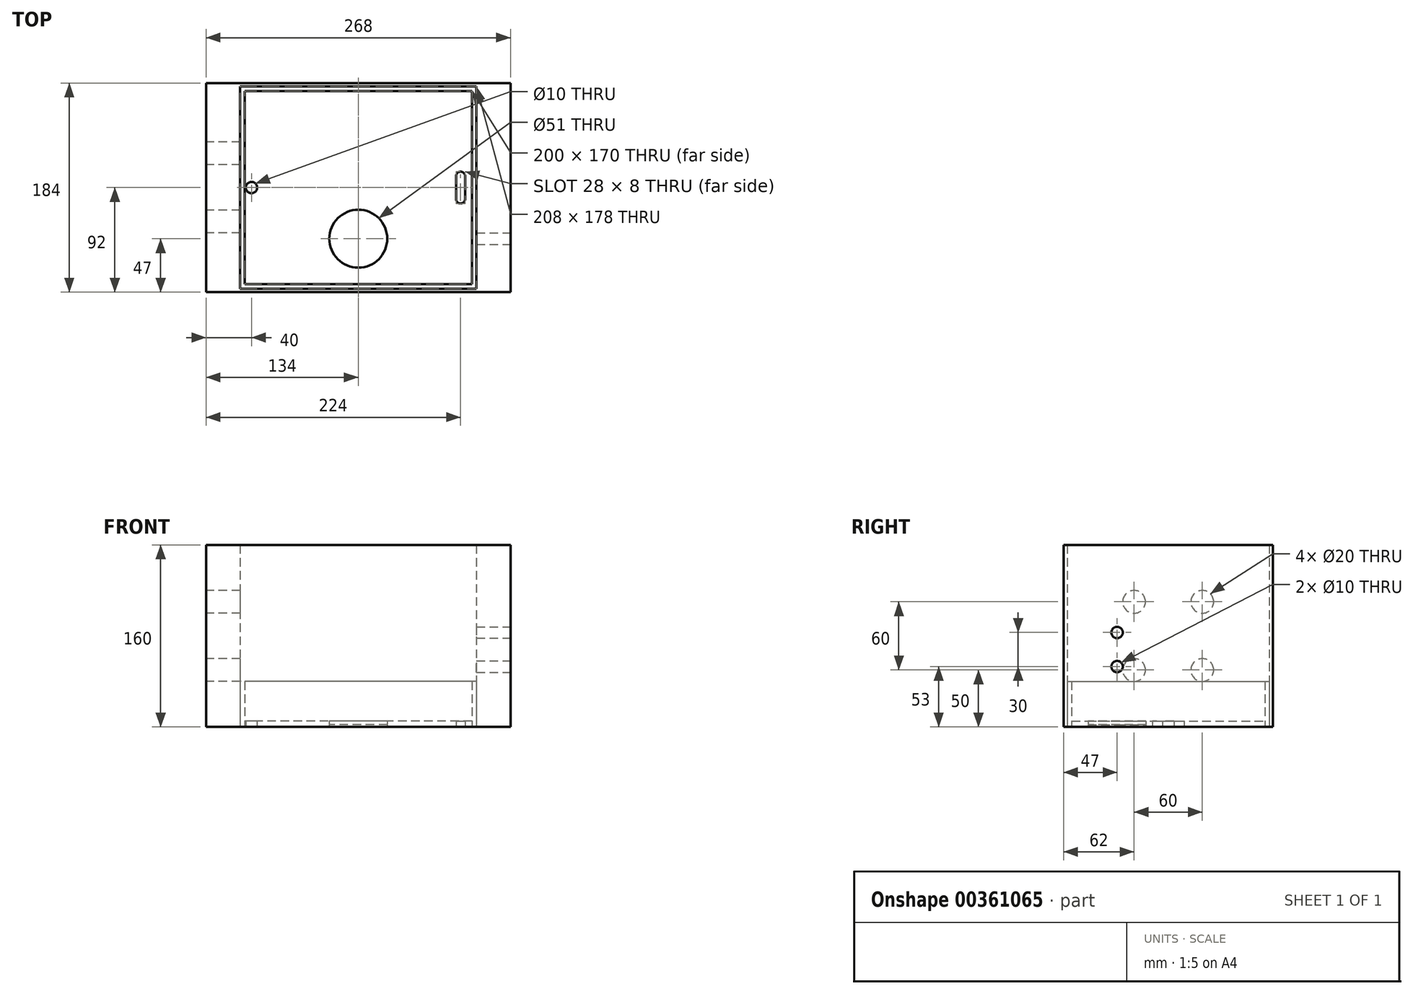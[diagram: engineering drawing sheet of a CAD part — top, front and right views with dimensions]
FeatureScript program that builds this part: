
annotation { "Feature Type Name" : "Feature", "Feature Type Description" : "" }
export const myFeature = defineFeature(function(context is Context, id is Id, definition is map)
    precondition{}
    {
        {
            var Q0;
            Q0=qCreatedBy(makeId("Top.planeOp"),FACE);
            var sketch = newSketch(context, id + "F0", { "sketchPlane" : qUnion([Q0])});
            skLineSegment(sketch, "E0.bottom", {"start": v(134, -47) * mm, "end": v(-134, -47) * mm});
            skLineSegment(sketch, "E0.top", {"start": v(134, 137) * mm, "end": v(-134, 137) * mm});
            skPoint(sketch, "E0.middle", {"position": v(0, 0) * mm});
            skCircle(sketch, "E1", {"center": v(0, 0) * mm, "radius": 25.5 * mm});
            skLineSegment(sketch, "E2.0", {"start": v(-100, -40) * mm, "end": v(-100, 130) * mm});
            skLineSegment(sketch, "E2.1", {"start": v(100, -40) * mm, "end": v(-100, -40) * mm});
            skLineSegment(sketch, "E2.2", {"start": v(100, -40) * mm, "end": v(100, 130) * mm});
            skLineSegment(sketch, "E2.3", {"start": v(100, 130) * mm, "end": v(-100, 130) * mm});
            skLineSegment(sketch, "E3.0", {"start": v(104, 134) * mm, "end": v(-104, 134) * mm});
            skLineSegment(sketch, "E3.1", {"start": v(104, -44) * mm, "end": v(104, 134) * mm});
            skLineSegment(sketch, "E3.2", {"start": v(104, -44) * mm, "end": v(-104, -44) * mm});
            skLineSegment(sketch, "E3.3", {"start": v(-104, -44) * mm, "end": v(-104, 134) * mm});
            skLineSegment(sketch, "E4", {"start": v(134, -47) * mm, "end": v(134, 137) * mm});
            skLineSegment(sketch, "E5", {"start": v(134, 45) * mm, "end": v(94, 45) * mm});
            skPoint(sketch, "E5.endSnap0", {"position": v(134, 45) * mm});
            skLineSegment(sketch, "E6", {"start": v(94, 45) * mm, "end": v(94, 35) * mm});
            skLineSegment(sketch, "E7", {"start": v(94, 45) * mm, "end": v(94, 55) * mm});
            skArc(sketch, "E8", {"start": v(94, 35) * mm, "mid": v(90, 31) * mm, "end": v(86, 35) * mm});
            skArc(sketch, "E9", {"start": v(94, 55) * mm, "mid": v(90, 59) * mm, "end": v(86, 55) * mm});
            skLineSegment(sketch, "E10", {"start": v(86, 35) * mm, "end": v(86, 55) * mm});
            skLineSegment(sketch, "E11", {"start": v(-134, 137) * mm, "end": v(-134, -47) * mm});
            skPoint(sketch, "E12", {"position": v(-94, 45) * mm});
            skCircle(sketch, "E13", {"center": v(-94, 45) * mm, "radius": 5 * mm});
            skSolve(sketch);
        }
        {
            var Q0;
            Q0=makeQuery(id+"F0.imprint","IMPRINT",FACE,{"disambiguationData":[TD([[makeQuery(id+"F0.imprint","IMPRINT",EDGE,{"derivedFrom":sQuery(id+"F0.wireOp",EDGE,"E1")}),1.0]])]});
            extrude(context, id + "F1", {"entities" : qUnion([Q0]), "depth" : 2 * mm});
        }
        {
            var Q0;
            Q0=makeQuery(id+"F0.imprint","IMPRINT",FACE,{"disambiguationData":[TD([[makeQuery(id+"F0.imprint","IMPRINT",EDGE,{"derivedFrom":sQuery(id+"F0.wireOp",EDGE,"E1")}),-1.0]])]});
            var Q1;
            Q1=makeQuery(id+"F0.imprint","IMPRINT",FACE,{"disambiguationData":[TD([[makeQuery(id+"F0.imprint","IMPRINT",EDGE,{"derivedFrom":sQuery(id+"F0.wireOp",EDGE,"wDK2D86D-5Smb-rO2F-uM56-sWFtckQkBcLd")}),1.0]])]});
            extrude(context, id + "F2", {"entities" : qUnion([Q0, Q1]), "depth" : 5 * mm});
        }
        {
            var Q0;
            {var subQ5=sQuery(id+"F0.wireOp",EDGE,"E0.bottom");Q0=makeQuery(id+"F0.imprint","IMPRINT",FACE,{"disambiguationData":[TD([[makeQuery(id+"F0.imprint","IMPRINT",EDGE,{"derivedFrom":subQ5}),-1.0]])]});}
            extrude(context, id + "F3", {"entities" : qUnion([Q0]), "depth" : 160 * mm});
        }
        {
            var Q0;
            Q0=makeQuery(id+"F0.imprint","IMPRINT",FACE,{"disambiguationData":[TD([[makeQuery(id+"F0.imprint","IMPRINT",EDGE,{"derivedFrom":sQuery(id+"F0.wireOp",EDGE,"E2.0")}),1.0]])]});
            extrude(context, id + "F4", {"entities" : qUnion([Q0]), "depth" : 40 * mm});
        }
        {
            var Q0;
            Q0=makeQuery(id+"F3.opExtrude","SWEPT_FACE",FACE,{"disambiguationData":[OSD([sQuery(id+"F0.wireOp",EDGE,"E4")])]});
            var sketch = newSketch(context, id + "F5", { "sketchPlane" : qUnion([Q0])});
            skLineSegment(sketch, "E14", {"start": v(45, 0) * mm, "end": v(45, 35) * mm});
            skLineSegment(sketch, "E15", {"start": v(45, 35) * mm, "end": v(45, 45) * mm});
            skPoint(sketch, "E16.middle", {"position": v(0, 53) * mm});
            skPoint(sketch, "E17.middle", {"position": v(0, 83) * mm});
            skCircle(sketch, "E18", {"center": v(0, 83) * mm, "radius": 5 * mm});
            skCircle(sketch, "E19", {"center": v(0, 53) * mm, "radius": 5 * mm});
            skSolve(sketch);
        }
        {
            var Q0;
            Q0=makeQuery(id+"F5.imprint","IMPRINT",FACE,{"disambiguationData":[TD([[makeQuery(id+"F5.imprint","IMPRINT",EDGE,{"derivedFrom":sQuery(id+"F5.wireOp",EDGE,"E18")}),1.0]])]});
            extrude(context, id + "F6", {"entities" : qUnion([Q0]), "operationType" : NewBodyOperationType.REMOVE, "oppositeDirection" : true, "depth" : 30.3 * mm});
        }
        {
            var Q0;
            Q0=makeQuery(id+"F5.imprint","IMPRINT",FACE,{"disambiguationData":[TD([[makeQuery(id+"F5.imprint","IMPRINT",EDGE,{"derivedFrom":sQuery(id+"F5.wireOp",EDGE,"E19")}),1.0]])]});
            extrude(context, id + "F7", {"entities" : qUnion([Q0]), "operationType" : NewBodyOperationType.REMOVE, "oppositeDirection" : true, "depth" : 30 * mm});
        }
        {
            var Q0;
            Q0=makeQuery(id+"F0.imprint","IMPRINT",FACE,{"disambiguationData":[TD([[makeQuery(id+"F0.imprint","IMPRINT",EDGE,{"derivedFrom":sQuery(id+"F0.wireOp",EDGE,"E6")}),-1.0]])]});
            extrude(context, id + "F8", {"entities" : qUnion([Q0]), "operationType" : NewBodyOperationType.REMOVE, "depth" : 10 * mm});
        }
        {
            var Q0;
            Q0=makeQuery(id+"F3.opExtrude","SWEPT_FACE",FACE,{"disambiguationData":[OSD([sQuery(id+"F0.wireOp",EDGE,"E11")])]});
            var sketch = newSketch(context, id + "F9", { "sketchPlane" : qUnion([Q0])});
            skLineSegment(sketch, "E20", {"start": v(-45, 0) * mm, "end": v(-45, 160) * mm, "construction": true});
            skLineSegment(sketch, "E21", {"start": v(-137, 80) * mm, "end": v(47, 80) * mm, "construction": true});
            skPoint(sketch, "E22", {"position": v(-45, 80) * mm});
            skPoint(sketch, "E23", {"position": v(-45, 110) * mm});
            skPoint(sketch, "E24", {"position": v(-45, 50) * mm});
            skPoint(sketch, "E25", {"position": v(-15, 80) * mm});
            skPoint(sketch, "E26", {"position": v(-75, 80) * mm});
            skCircle(sketch, "E27", {"center": v(-15, 50) * mm, "radius": 10 * mm});
            skCircle(sketch, "E28", {"center": v(-75, 50) * mm, "radius": 10 * mm});
            skCircle(sketch, "E29", {"center": v(-75, 110) * mm, "radius": 10 * mm});
            skCircle(sketch, "E30", {"center": v(-15, 110) * mm, "radius": 10 * mm});
            skSolve(sketch);
        }
        {
            var Q0;
            Q0=makeQuery(id+"F9.imprint","IMPRINT",FACE,{"disambiguationData":[TD([[makeQuery(id+"F9.imprint","IMPRINT",EDGE,{"derivedFrom":sQuery(id+"F9.wireOp",EDGE,"E29")}),1.0]])]});
            var Q1;
            Q1=makeQuery(id+"F9.imprint","IMPRINT",FACE,{"disambiguationData":[TD([[makeQuery(id+"F9.imprint","IMPRINT",EDGE,{"derivedFrom":sQuery(id+"F9.wireOp",EDGE,"E30")}),1.0]])]});
            var Q2;
            Q2=makeQuery(id+"F9.imprint","IMPRINT",FACE,{"disambiguationData":[TD([[makeQuery(id+"F9.imprint","IMPRINT",EDGE,{"derivedFrom":sQuery(id+"F9.wireOp",EDGE,"E28")}),1.0]])]});
            var Q3;
            Q3=makeQuery(id+"F9.imprint","IMPRINT",FACE,{"disambiguationData":[TD([[makeQuery(id+"F9.imprint","IMPRINT",EDGE,{"derivedFrom":sQuery(id+"F9.wireOp",EDGE,"E27")}),1.0]])]});
            var Q4;
            Q4=makeQuery(id+"F3.opExtrude","SWEPT_FACE",FACE,{"disambiguationData":[OSD([sQuery(id+"F0.wireOp",EDGE,"E3.3")])]});
            extrude(context, id + "F10", {"entities" : qUnion([Q0, Q1, Q2, Q3]), "operationType" : NewBodyOperationType.REMOVE, "endBound" : BoundingType.UP_TO_SURFACE, "oppositeDirection" : true, "endBoundEntityFace" : qUnion([Q4]), "depth" : 25 * mm});
        }
    });
